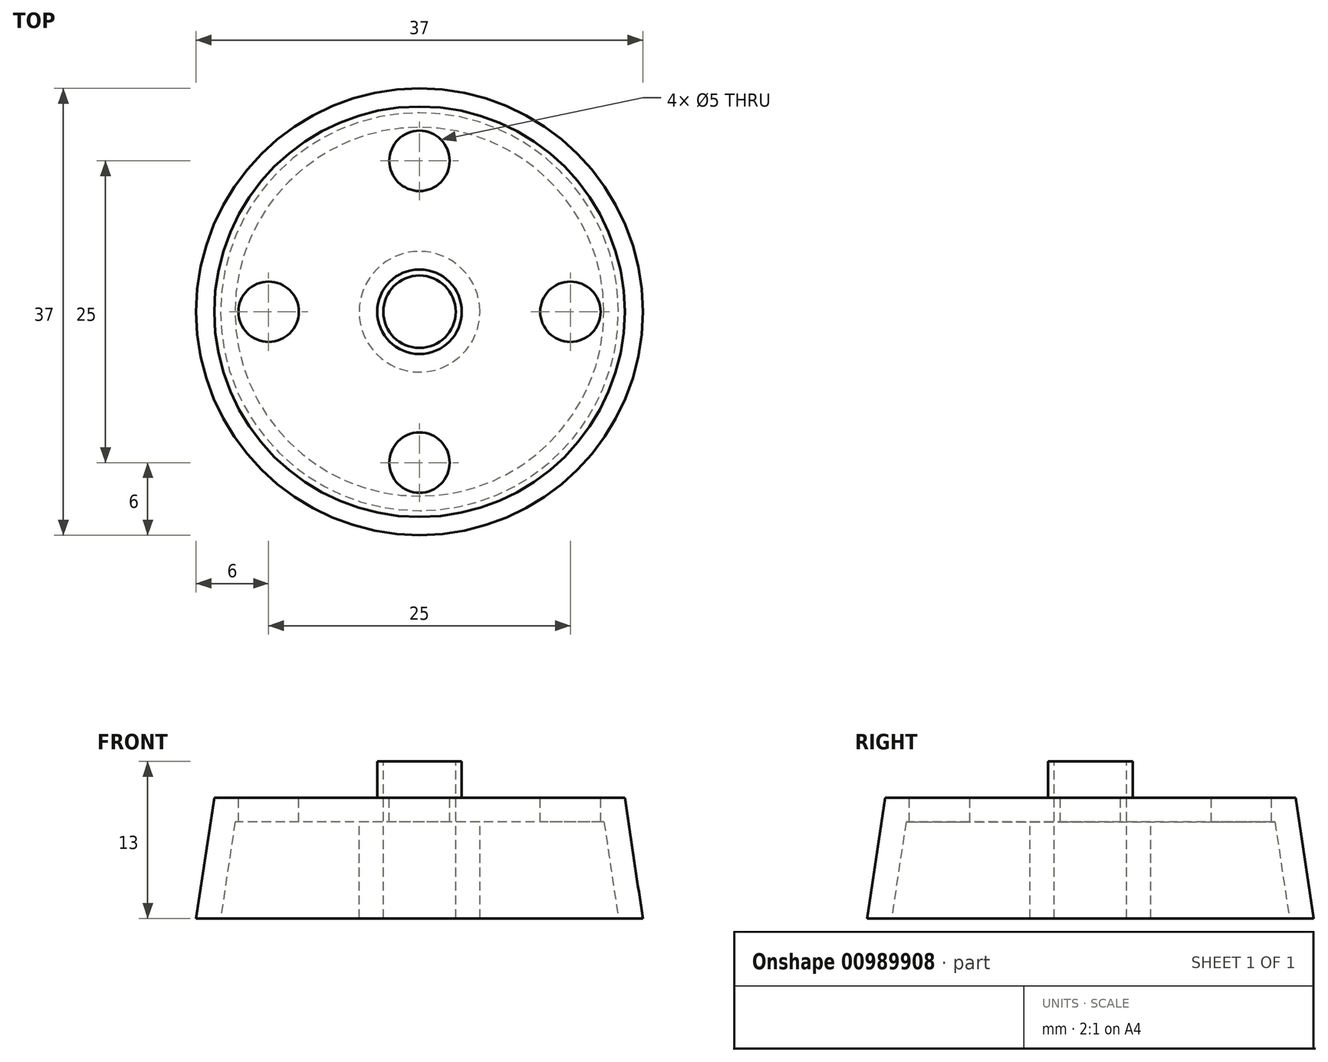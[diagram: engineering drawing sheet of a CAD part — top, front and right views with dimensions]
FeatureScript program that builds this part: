
annotation { "Feature Type Name" : "Feature", "Feature Type Description" : "" }
export const myFeature = defineFeature(function(context is Context, id is Id, definition is map)
    precondition{}
    {
        {
            var Q0;
            Q0=qCreatedBy(makeId("Top.planeOp"),FACE);
            var sketch = newSketch(context, id + "F0", { "sketchPlane" : qUnion([Q0])});
            skCircle(sketch, "E0", {"center": v(0, 0) * mm, "radius": 18.5 * mm});
            skSolve(sketch);
        }
        {
            var Q0;
            Q0=qCreatedBy(makeId("Top.planeOp"),FACE);
            cPlane(context, id + "F1", {"entities" : qUnion([Q0]), "cplaneType" : CPlaneType.OFFSET, "offset" : 10 * mm, "width" : 150 * mm, "height" : 150 * mm});
        }
        {
            var Q0;
            Q0=qCreatedBy(id+"F1.planeOp",FACE);
            var sketch = newSketch(context, id + "F2", { "sketchPlane" : qUnion([Q0])});
            skCircle(sketch, "E1", {"center": v(0, 0) * mm, "radius": 17 * mm});
            skSolve(sketch);
        }
        {
            var Q0;
            Q0=makeQuery(id+"F0.imprint","IMPRINT",FACE,{"disambiguationData":[TD([[makeQuery(id+"F0.imprint","IMPRINT",EDGE,{"derivedFrom":sQuery(id+"F0.wireOp",EDGE,"E0")}),1.0]])]});
            var Q1;
            Q1=makeQuery(id+"F2.imprint","IMPRINT",FACE,{"disambiguationData":[TD([[makeQuery(id+"F2.imprint","IMPRINT",EDGE,{"derivedFrom":sQuery(id+"F2.wireOp",EDGE,"E1")}),1.0]])]});
            loft(context, id + "F3", {"sheetProfilesArray" : [{ "sheetProfileEntities" : qUnion([Q0]) }, { "sheetProfileEntities" : qUnion([Q1]) }]});
        }
        {
            var Q0;
            Q0=makeQuery(id+"F3.opLoft","CAP_FACE",FACE,{"disambiguationData":[OSD([makeQuery(id+"F2.imprint","IMPRINT",FACE,{"disambiguationData":[TD([[makeQuery(id+"F2.imprint","IMPRINT",EDGE,{"derivedFrom":sQuery(id+"F2.wireOp",EDGE,"E1")}),1.0]])]})])],"isStart":true});
            var sketch = newSketch(context, id + "F4", { "sketchPlane" : qUnion([Q0])});
            skCircle(sketch, "E2", {"center": v(0, 0) * mm, "radius": 12.5 * mm, "construction": true});
            skLineSegment(sketch, "E3", {"start": v(-17, 0) * mm, "end": v(17, 0) * mm, "construction": true});
            skLineSegment(sketch, "E4", {"start": v(0, -17) * mm, "end": v(0, 17) * mm, "construction": true});
            skCircle(sketch, "E5", {"center": v(12.5, 0) * mm, "radius": 2.5 * mm});
            skCircle(sketch, "E6", {"center": v(-12.5, 0) * mm, "radius": 2.5 * mm});
            skCircle(sketch, "E7", {"center": v(0, -12.5) * mm, "radius": 2.5 * mm});
            skCircle(sketch, "E8", {"center": v(0, 12.5) * mm, "radius": 2.5 * mm});
            skCircle(sketch, "E9", {"center": v(0, 0) * mm, "radius": 3 * mm});
            skCircle(sketch, "E10", {"center": v(0, 0) * mm, "radius": 3.5 * mm});
            skSolve(sketch);
        }
        {
            var Q0;
            Q0=makeQuery(id+"F4.imprint","IMPRINT",FACE,{"disambiguationData":[TD([[makeQuery(id+"F4.imprint","IMPRINT",EDGE,{"derivedFrom":sQuery(id+"F4.wireOp",EDGE,"E6")}),1.0]])]});
            var Q1;
            Q1=makeQuery(id+"F4.imprint","IMPRINT",FACE,{"disambiguationData":[TD([[makeQuery(id+"F4.imprint","IMPRINT",EDGE,{"derivedFrom":sQuery(id+"F4.wireOp",EDGE,"E8")}),1.0]])]});
            var Q2;
            Q2=makeQuery(id+"F4.imprint","IMPRINT",FACE,{"disambiguationData":[TD([[makeQuery(id+"F4.imprint","IMPRINT",EDGE,{"derivedFrom":sQuery(id+"F4.wireOp",EDGE,"E5")}),1.0]])]});
            var Q3;
            Q3=makeQuery(id+"F4.imprint","IMPRINT",FACE,{"disambiguationData":[TD([[makeQuery(id+"F4.imprint","IMPRINT",EDGE,{"derivedFrom":sQuery(id+"F4.wireOp",EDGE,"E7")}),1.0]])]});
            var Q4;
            Q4=makeQuery(id+"F4.imprint","IMPRINT",FACE,{"disambiguationData":[TD([[makeQuery(id+"F4.imprint","IMPRINT",EDGE,{"derivedFrom":sQuery(id+"F4.wireOp",EDGE,"E9")}),1.0]])]});
            var Q5;
            Q5=sQuery(id+"F4.wireOp",EDGE,"E6");
            var Q6;
            Q6=sQuery(id+"F4.wireOp",EDGE,"E8");
            var Q7;
            Q7=sQuery(id+"F4.wireOp",EDGE,"E5");
            var Q8;
            Q8=sQuery(id+"F4.wireOp",EDGE,"E7");
            extrude(context, id + "F5", {"entities" : qUnion([Q0, Q1, Q2, Q3, Q4]), "operationType" : NewBodyOperationType.REMOVE, "surfaceEntities" : qUnion([Q5, Q6, Q7, Q8]), "oppositeDirection" : true, "depth" : 10 * mm, "offsetDistance" : 25 * mm});
        }
        {
            var Q0;
            Q0=makeQuery(id+"F5.boolean.opBoolean","COPY",FACE,{"derivedFrom":makeQuery(id+"F5.opExtrude","SWEPT_FACE",FACE,{"disambiguationData":[OSD([sQuery(id+"F4.wireOp",EDGE,"E7")])]})});
            var Q1;
            Q1=makeQuery(id+"F3.opLoft","CAP_FACE",FACE,{"disambiguationData":[OSD([makeQuery(id+"F0.imprint","IMPRINT",FACE,{"disambiguationData":[TD([[makeQuery(id+"F0.imprint","IMPRINT",EDGE,{"derivedFrom":sQuery(id+"F0.wireOp",EDGE,"E0")}),1.0]])]})])],"isStart":true});
            var Q2;
            Q2=makeQuery(id+"F5.boolean.opBoolean","COPY",FACE,{"derivedFrom":makeQuery(id+"F5.opExtrude","SWEPT_FACE",FACE,{"disambiguationData":[OSD([sQuery(id+"F4.wireOp",EDGE,"E6")])]})});
            var Q3;
            Q3=makeQuery(id+"F5.boolean.opBoolean","COPY",FACE,{"derivedFrom":makeQuery(id+"F5.opExtrude","SWEPT_FACE",FACE,{"disambiguationData":[OSD([sQuery(id+"F4.wireOp",EDGE,"E8")])]})});
            var Q4;
            Q4=makeQuery(id+"F5.boolean.opBoolean","COPY",FACE,{"derivedFrom":makeQuery(id+"F5.opExtrude","SWEPT_FACE",FACE,{"disambiguationData":[OSD([sQuery(id+"F4.wireOp",EDGE,"E5")])]})});
            shell(context, id + "F6", {"entities" : qUnion([Q0, Q1, Q2, Q3, Q4]), "thickness" : 2 * mm});
        }
        {
            var Q0;
            Q0=makeQuery(id+"F4.imprint","IMPRINT",FACE,{"disambiguationData":[TD([[makeQuery(id+"F4.imprint","IMPRINT",EDGE,{"derivedFrom":sQuery(id+"F4.wireOp",EDGE,"E9")}),-1.0]])]});
            var Q1;
            Q1=sQuery(id+"F4.wireOp",EDGE,"E10");
            extrude(context, id + "F7", {"entities" : qUnion([Q0]), "operationType" : NewBodyOperationType.ADD, "surfaceEntities" : qUnion([Q1]), "depth" : 3 * mm, "offsetDistance" : 25 * mm});
        }
    });
